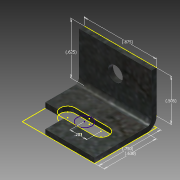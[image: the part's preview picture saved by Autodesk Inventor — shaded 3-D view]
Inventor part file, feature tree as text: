
AUTODESK INVENTOR PART (.ipt)
format: ipt  version: 2015 (Build 190159000, 159)  size: 193,024 bytes
history: native  units: in
note: dims shown in document units (in); Inventor stores cm internally (conversion verified against a paired STEP export)
features: sketch x8, sheet_metal_op x4, other x4, projected_geometry x4, hole x1
ambient origin geometry x8: Origin, YZ Plane, XZ Plane, XY Plane, X Axis, Y Axis, Z Axis, Center Point
bodies: Solid1 (feature_tree)
feature tree (21):
  sheet_metal_op  "Face1"
  sheet_metal_op  "Flange1"
  sketch  "Sketch3"  dims[d3=0.06in]
  hole  "Hole1"  [1 undecoded]
  sketch  "Sketch7"  dims[d5=0.12in]
  sketch  "Sketch8"  dims[d6=0.06in]
  sketch  "Sketch9"  dims[d7=0.625in d8=90.0deg d9=0.06in]
  sketch  "Sketch1"  dims[d0=0.875in d1=0.75in]
  other  "Plate1"
  sketch  "Sketch2"  dims[d2=0.06in]
  other  "Plate2"
  sheet_metal_op  "Bend1"
  sheet_metal_op  "Corner1"
  projected_geometry  "Projected Loop1"
  sketch  "Sketch4"  dims[d4=0.03in]
  projected_geometry  "Projected Loop2"
  projected_geometry  "Projected Loop3"
  projected_geometry  "Projected Loop4"
  sketch  "Sketch10"  dims[d10=0.24in d11=0.06in d12=0.06in d13=0.63in d14=0.875in d15=0.875in d16=0.505in d17=0.177in d18=0.75in d19=0.332in d20=0.25in d21=0.5635in d22=0.06in d23=0.8108in d24=0.177in d25=0.146in d26=0.06in d27=0.0in d28=0.625in d29=0.505in d30=0.875in d31=0.75in d32=0.63in d34=0.203in d35=0.281in d36=0.281in d39=0.281in d40=0.06in d41=0.0in]
  other  "Cut1"
  other  "Cut3"
note: 1 required parameter value undecoded (feature->parameter linkage not recoverable at this tier; creation-order binding heuristic only, values carry confidence <= 0.55)
